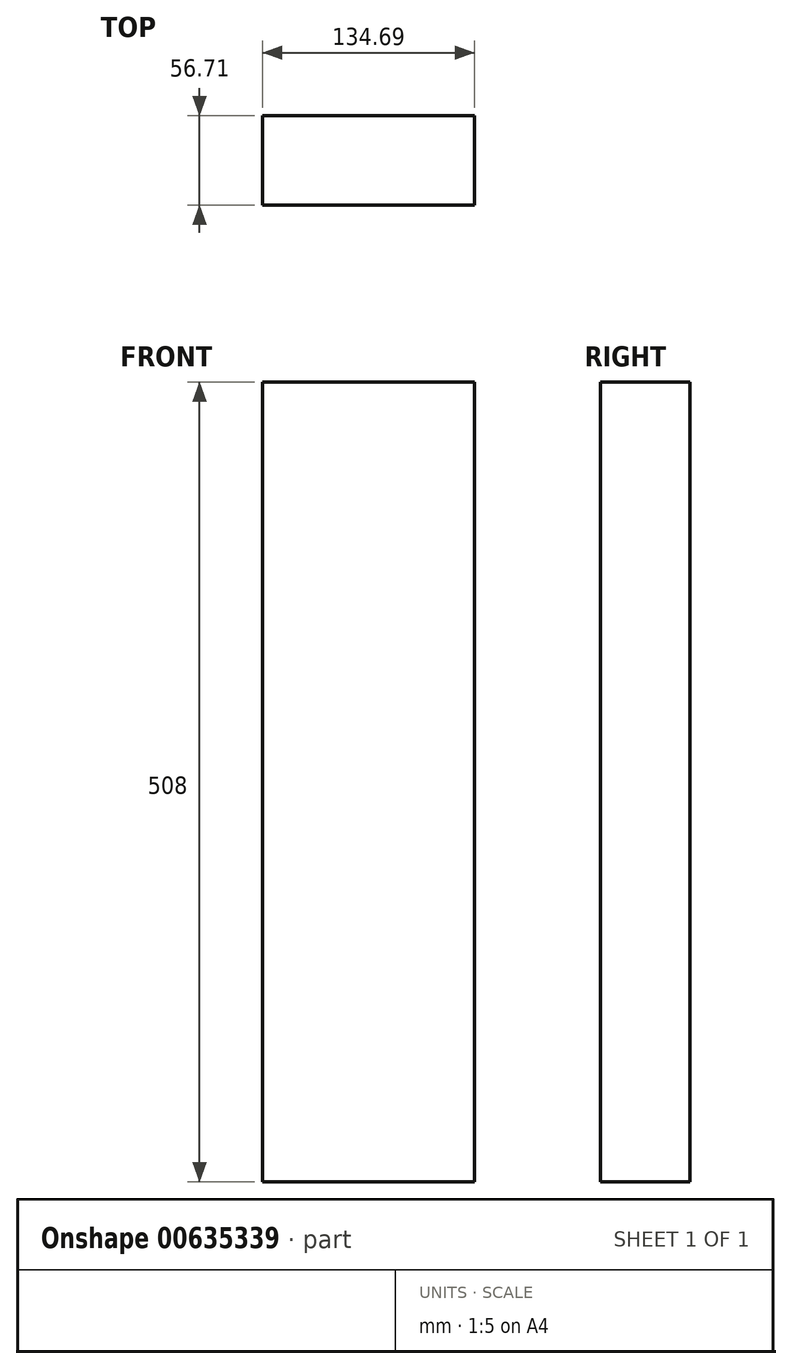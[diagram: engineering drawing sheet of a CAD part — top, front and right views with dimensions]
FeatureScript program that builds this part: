
annotation { "Feature Type Name" : "Feature", "Feature Type Description" : "" }
export const myFeature = defineFeature(function(context is Context, id is Id, definition is map)
    precondition{}
    {
        {
            var Q0;
            Q0=qCreatedBy(makeId("Top.planeOp"),FACE);
            var sketch = newSketch(context, id + "F0", { "sketchPlane" : qUnion([Q0])});
            skLineSegment(sketch, "E0.bottom", {"start": v(0, 0) * mm, "end": v(134.69, 0) * mm});
            skLineSegment(sketch, "E0.top", {"start": v(0, -56.71) * mm, "end": v(134.69, -56.71) * mm});
            skLineSegment(sketch, "E0.left", {"start": v(0, 0) * mm, "end": v(0, -56.71) * mm});
            skLineSegment(sketch, "E0.right", {"start": v(134.69, 0) * mm, "end": v(134.69, -56.71) * mm});
            skSolve(sketch);
        }
        {
            var Q0;
            Q0 = qSketchRegion(id + "F0", true);
            extrude(context, id + "F1", {"entities" : qUnion([Q0]), "oppositeDirection" : true, "depth" : 508 * mm, "offsetDistance" : 25.4 * mm});
        }
    });
